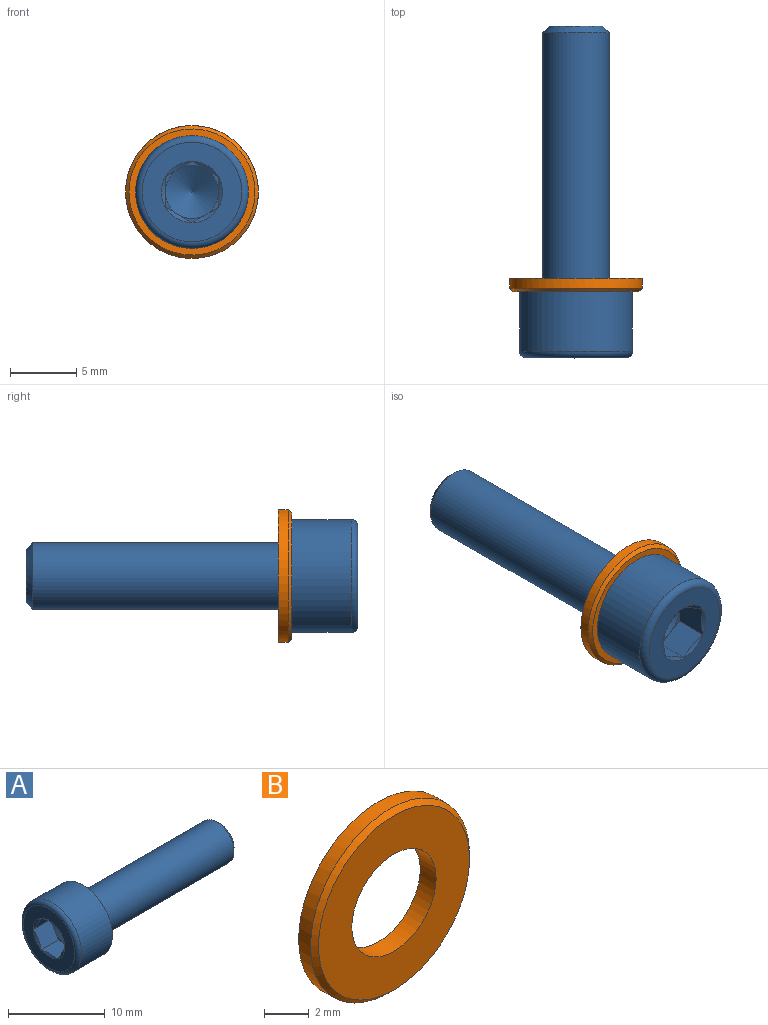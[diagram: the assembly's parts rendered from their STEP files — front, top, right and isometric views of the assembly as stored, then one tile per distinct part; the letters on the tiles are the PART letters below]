
ASSEMBLY  parts=2 mates=1
PART A: 24 faces, bbox 25x9.2x9.2 mm
  f0: plane 1.73x1mm, normal (-1,0,0), area 0.2mm2, adj f16,f17,f23
  f1: plane 2x0.58mm, normal (-1,0,0), area 0.2mm2, adj f17,f18,f23
  f2: plane 1.73x1mm, normal (-1,0,0), area 0.2mm2, adj f18,f19,f23
  f3: plane 1.73x1mm, normal (-1,0,0), area 0.2mm2, adj f19,f20,f23
  f4: plane 2x0.58mm, normal (-1,0,0), area 0.2mm2, adj f20,f21,f23
  f5: cone r=2.31mm half-angle=60deg, axis (-1,0,0), area 3.4mm2, adj f15,f16,f17,f18,f19,f20,f21
  f6: cone r=2.51mm half-angle=20.6deg, axis (-1,0,0), area 6.9mm2, adj f7,f11
  f7: torus R=2.7mm, axis (1,0,0), area 1.1mm2, adj f6,f10
  f8: plane 4.02x4.02mm, normal (1,0,0), area 12.7mm2, adj f9
  f9: cone r=2.5mm half-angle=45deg, axis (-1,0,0), area 9.8mm2, adj f8,f10
  f10: cylinder r=2.5mm len=18.91mm, axis (1,0,0), area 297mm2, adj f7,f9
  f11: torus R=2.85mm, axis (1,0,0), area 4.2mm2, adj f6,f13
  f12: cylinder r=4.25mm len=8.5mm, axis (1,0,0), area 120.2mm2, adj f13,f14
  f13: plane 8.5x8.5mm, normal (1,0,0), area 31.2mm2, adj f11,f12
  f14: torus R=3.75mm, axis (1,0,0), area 20.1mm2, adj f12,f15
  f15: plane 7.5x7.5mm, normal (-1,0,0), area 27.4mm2, adj f5,f14
  f16: plane 2.5x2.31mm, normal (0,0,-1), area 5.5mm2, adj f0,f5,f17,f21,f22
  f17: plane 2.5x2mm, normal (0,0.87,-0.5), area 5.5mm2, adj f0,f1,f5,f16,f18
  f18: plane 2.5x2mm, normal (0,0.87,0.5), area 5.5mm2, adj f1,f2,f5,f17,f19
  f19: plane 2.5x2.31mm, normal (0,0,1), area 5.5mm2, adj f2,f3,f5,f18,f20
  f20: plane 2.5x2mm, normal (0,-0.87,0.5), area 5.5mm2, adj f3,f4,f5,f19,f21
  f21: plane 2.5x2mm, normal (0,-0.87,-0.5), area 5.5mm2, adj f4,f5,f16,f20,f22
  f22: plane 1.73x1mm, normal (-1,0,0), area 0.2mm2, adj f16,f21,f23
  f23: cone r=2mm half-angle=60deg, axis (-1,0,0), area 14.5mm2, adj f0,f1,f2,f3,f4,f22
PART B: 5 faces, bbox 10x1x10 mm
  f0: cylinder r=2.65mm len=5.3mm, axis (0,1,0), area 16.7mm2, adj f2,f3
  f1: cylinder r=5mm len=10mm, axis (0,1,0), area 23.6mm2, adj f3,f4
  f2: plane 9.5x9.5mm, normal (0,-1,0), area 48.8mm2, adj f0,f4
  f3: plane 10x10mm, normal (0,1,0), area 56.5mm2, adj f0,f1
  f4: cone r=5mm half-angle=45deg, axis (0,1,0), area 10.8mm2, adj f1,f2
PLACE A rot(axis=(-0.58,-0.58,0.58),120deg) t=(0,-1,0)mm
PLACE B at identity fixed
MATE fastened A.f5 <-> B.f0  axis (0,1,0) through (0,-1,0)mm
